# Revit family: Gira_536127
name_source: partatom
category: Elektroinstallationen
revit_build: Autodesk Revit 2017 (Build: 20160225_1515(x64)
units: mm (PartAtom-declared; Revit-internal decimal feet)

## family parameters
Basisbauteil = Fläche
Beim Laden mit Abzugskörper schneiden = Nein
Bemaßung runder Anschluss = Durchmesser verwenden
Beschriftungsausrichtung beibehalten = Nein
Gemeinsam genutzt = Nein
Raumberechnungspunkt = Nein
Teiletyp = Normal

## types (1)
- S3000 Bedienaufs. Pfeilsymbole System 55 Reinweiß m
    Anwendung = Steuern elektrischer Verbraucher
    Anzahl der Betätigungspunkte = 2
    Anzahl der Tasten = 1
    Ausführung der Oberfläche = matt
    Bauelement = Sys55_Abdeckung_Schalten und Tasten
    Beschreibung = System 3000 Bedienaufsatz Pfeilsymbole  Reinweiß seidenmatt
    Farbe = weiß
    GTIN = 4010337027300
    Geeignet für Dimmeinsatz = Nein
    Geeignet für Jalousieeinsatz = Ja
    Geeignet für Schalteinsatz = Nein
    HAN = 536127
    Halogenfrei = Ja
    HeinzeBIM = https://bimportal.heinze.de
    Hersteller = Gira
    Kategorie = Bedienelement intelligent
    Mit Abdeckung = Ja
    Mit LED-Anzeige = Nein
    Name = S3000 Bedienaufs. Pfeilsymbole System 55 Reinweiß m
    Oberfläche = sonstige
    RAL-Nummer (ähnlich) = 9010
    Region = DE
    Transparent = Nein
    URL = http://katalog.gira.de
    Verfügbar = Ja
    Vorgabe-Ansicht = 1219 mm
    Werkstoff = sonstige
    Werkstoffgüte = sonstige

## geometry (parser evidence)
native form markers: Sweep x7
no freeform markers — native parametric forms only
